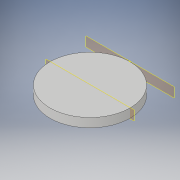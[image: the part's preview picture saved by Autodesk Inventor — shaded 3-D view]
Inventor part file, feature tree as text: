
AUTODESK INVENTOR PART (.ipt)
format: ipt  version: 2017.2 (Build 212233000, 233)  size: 103,424 bytes
history: native  units: in
note: dims shown in document units (in); Inventor stores cm internally (conversion verified against a paired STEP export)
features: sketch x3, extrude x2, plane x1
ambient origin geometry x8: Origin, YZ Plane, XZ Plane, XY Plane, X Axis, Y Axis, Z Axis, Center Point
bodies: Solid1 (feature_tree)
feature tree (6):
  extrude  "Extrusion1"  Depth=0.5in TaperAngle=0.0deg
  extrude  "Extrusion2"  Depth=0.375in TaperAngle=0.0deg
  plane  "Work Plane1"
  sketch  "Sketch3"
  sketch  "Sketch1"  dims[d0=4.5in d1=0.5in d2=0.0in]
  sketch  "Sketch2"  dims[d3=4.25in d4=0.375in d5=0.0in]
